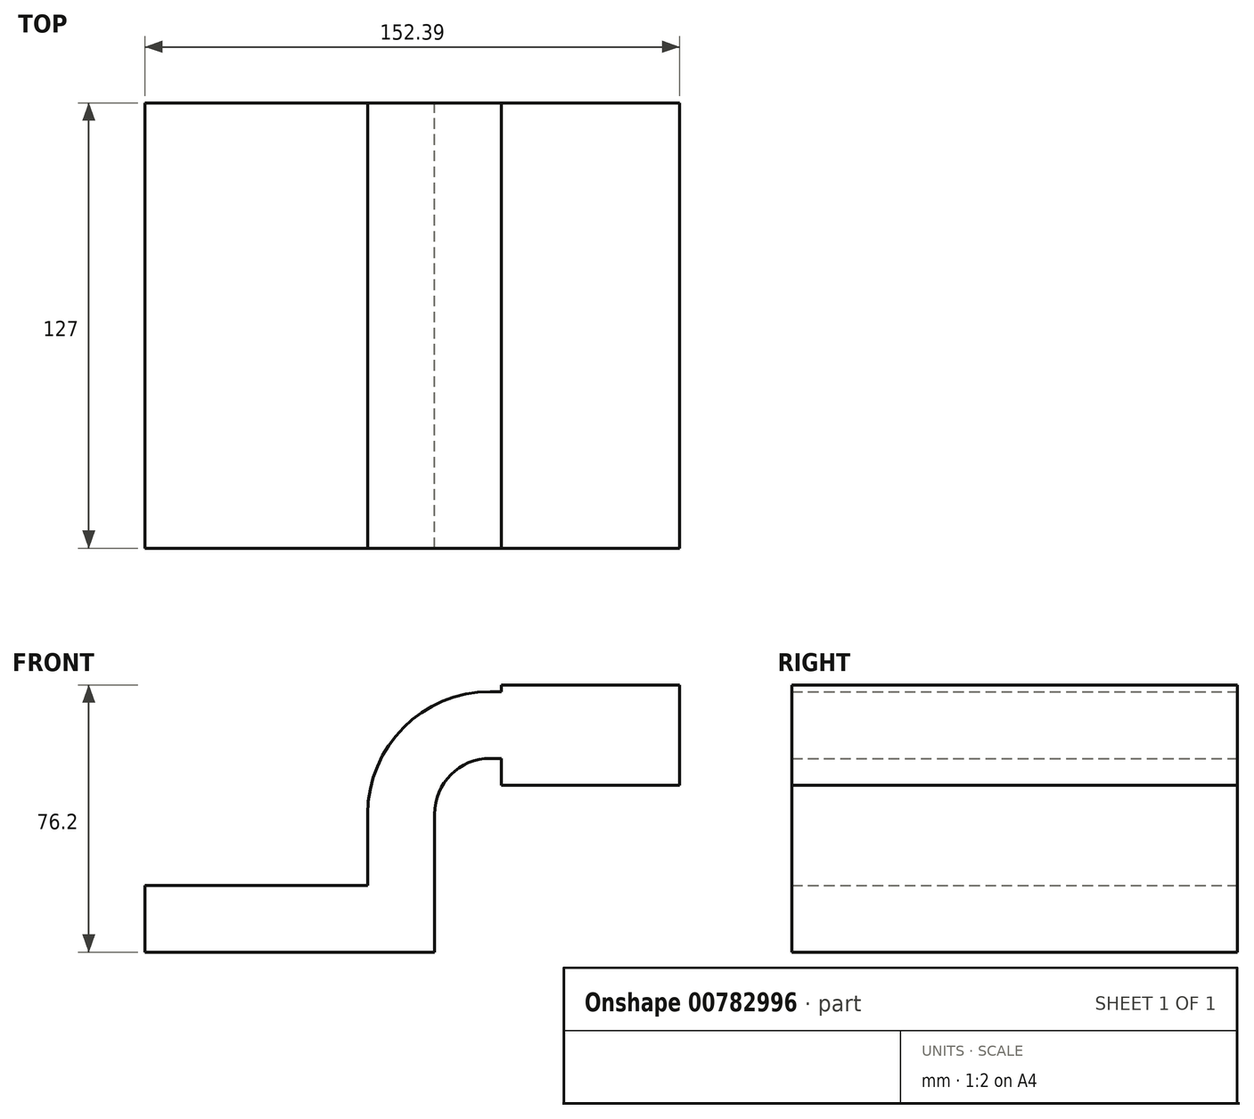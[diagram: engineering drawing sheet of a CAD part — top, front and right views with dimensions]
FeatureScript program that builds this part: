
annotation { "Feature Type Name" : "Feature", "Feature Type Description" : "" }
export const myFeature = defineFeature(function(context is Context, id is Id, definition is map)
    precondition{}
    {
        {
            var Q0;
            Q0=qCreatedBy(makeId("Front.planeOp"),FACE);
            var sketch = newSketch(context, id + "F0", { "sketchPlane" : qUnion([Q0])});
            skLineSegment(sketch, "E0.bottom", {"start": v(41.28, -9.52) * mm, "end": v(-41.28, -9.53) * mm});
            skLineSegment(sketch, "E0.top", {"start": v(41.28, 9.53) * mm, "end": v(-41.28, 9.52) * mm});
            skLineSegment(sketch, "E0.left", {"start": v(41.28, -9.52) * mm, "end": v(41.28, 9.53) * mm});
            skLineSegment(sketch, "E0.right", {"start": v(-41.28, -9.53) * mm, "end": v(-41.28, 9.52) * mm});
            skPoint(sketch, "E0.middle", {"position": v(0, 0) * mm});
            skLineSegment(sketch, "E1.bottom", {"start": v(111.12, 38.1) * mm, "end": v(60.32, 38.1) * mm});
            skLineSegment(sketch, "E1.top", {"start": v(111.12, 66.68) * mm, "end": v(60.32, 66.68) * mm});
            skLineSegment(sketch, "E1.left", {"start": v(111.12, 38.1) * mm, "end": v(111.12, 66.68) * mm});
            skLineSegment(sketch, "E1.right", {"start": v(60.32, 38.1) * mm, "end": v(60.32, 66.68) * mm});
            skPoint(sketch, "E1.middle", {"position": v(85.72, 52.39) * mm});
            skLineSegment(sketch, "E2", {"start": v(41.27, 9.53) * mm, "end": v(41.27, 29.85) * mm});
            skArc(sketch, "E3", {"start": v(41.27, 29.85) * mm, "mid": v(45.92, 41.07) * mm, "end": v(57.15, 45.72) * mm});
            skLineSegment(sketch, "E4", {"start": v(57.15, 45.72) * mm, "end": v(85.72, 45.72) * mm});
            skPoint(sketch, "E4.endSnap0", {"position": v(85.72, 38.1) * mm});
            skArc(sketch, "E5.0", {"start": v(22.23, 29.85) * mm, "mid": v(32.45, 54.54) * mm, "end": v(57.15, 64.77) * mm});
            skLineSegment(sketch, "E5.1", {"start": v(22.22, 9.53) * mm, "end": v(22.22, 29.85) * mm});
            skLineSegment(sketch, "E6.0", {"start": v(57.15, 64.77) * mm, "end": v(85.72, 64.77) * mm});
            skLineSegment(sketch, "E7", {"start": v(85.72, 38.1) * mm, "end": v(85.72, 66.68) * mm});
            skFitSpline(sketch, "E8", {"points": [v(-41.28, 9.52) * mm, v(57.15, 64.77) * mm], "startDerivative": vector(28.62, 132.5) * mm, "endDerivative": vector(134, -19.1) * mm});
            skSolve(sketch);
        }
        {
            var Q0;
            Q0=makeQuery(id+"F0.imprint","IMPRINT",FACE,{"disambiguationData":[TD([[makeQuery(id+"F0.imprint","IMPRINT",EDGE,{"derivedFrom":sQuery(id+"F0.wireOp",EDGE,"E5.0")}),1.0]])]});
            var Q1;
            {var subQ0=sQuery(id+"F0.wireOp",EDGE,"E1.right");var subQ1=sQuery(id+"F0.wireOp",EDGE,"E1.bottom");var subQ2=makeQuery(id+"F0.imprint","INTERSECT",VERTEX,{"derivedFrom":[subQ1,subQ0]});Q1=makeQuery(id+"F0.imprint","IMPRINT",FACE,{"disambiguationData":[TD([[makeQuery(id+"F0.imprint","IMPRINT",EDGE,{"disambiguationData":[TD([[subQ2,1.0]])],"derivedFrom":subQ1}),-1.0]])]});}
            var Q2;
            {var subQ0=sQuery(id+"F0.wireOp",EDGE,"E1.right");var subQ1=sQuery(id+"F0.wireOp",EDGE,"E1.top");var subQ2=makeQuery(id+"F0.imprint","INTERSECT",VERTEX,{"derivedFrom":[subQ1,subQ0]});Q2=makeQuery(id+"F0.imprint","IMPRINT",FACE,{"disambiguationData":[TD([[makeQuery(id+"F0.imprint","IMPRINT",EDGE,{"disambiguationData":[TD([[subQ2,1.0]])],"derivedFrom":subQ1}),1.0]])]});}
            var Q3;
            {var subQ1=sQuery(id+"F0.wireOp",EDGE,"E2");Q3=makeQuery(id+"F0.imprint","IMPRINT",FACE,{"disambiguationData":[TD([[makeQuery(id+"F0.imprint","IMPRINT",EDGE,{"derivedFrom":subQ1}),1.0]])]});}
            var Q4;
            {var subQ4=sQuery(id+"F0.wireOp",EDGE,"E1.left");Q4=makeQuery(id+"F0.imprint","IMPRINT",FACE,{"disambiguationData":[TD([[makeQuery(id+"F0.imprint","IMPRINT",EDGE,{"derivedFrom":subQ4}),1.0]])]});}
            var Q5;
            {var subQ0=sQuery(id+"F0.wireOp",EDGE,"E4");var subQ1=sQuery(id+"F0.wireOp",EDGE,"E1.right");var subQ2=makeQuery(id+"F0.imprint","INTERSECT",VERTEX,{"derivedFrom":[subQ1,subQ0]});Q5=makeQuery(id+"F0.imprint","IMPRINT",FACE,{"disambiguationData":[TD([[makeQuery(id+"F0.imprint","IMPRINT",EDGE,{"disambiguationData":[TD([[subQ2,-1.0]])],"derivedFrom":subQ1}),-1.0]])]});}
            var Q6;
            Q6=makeQuery(id+"F0.imprint","IMPRINT",FACE,{"disambiguationData":[TD([[makeQuery(id+"F0.imprint","IMPRINT",EDGE,{"derivedFrom":sQuery(id+"F0.wireOp",EDGE,"E0.bottom")}),-1.0]])]});
            extrude(context, id + "F1", {"entities" : qUnion([Q0, Q1, Q2, Q3, Q4, Q5, Q6]), "endBound" : BoundingType.SYMMETRIC, "depth" : 127 * mm, "offsetDistance" : 25.4 * mm});
        }
    });
